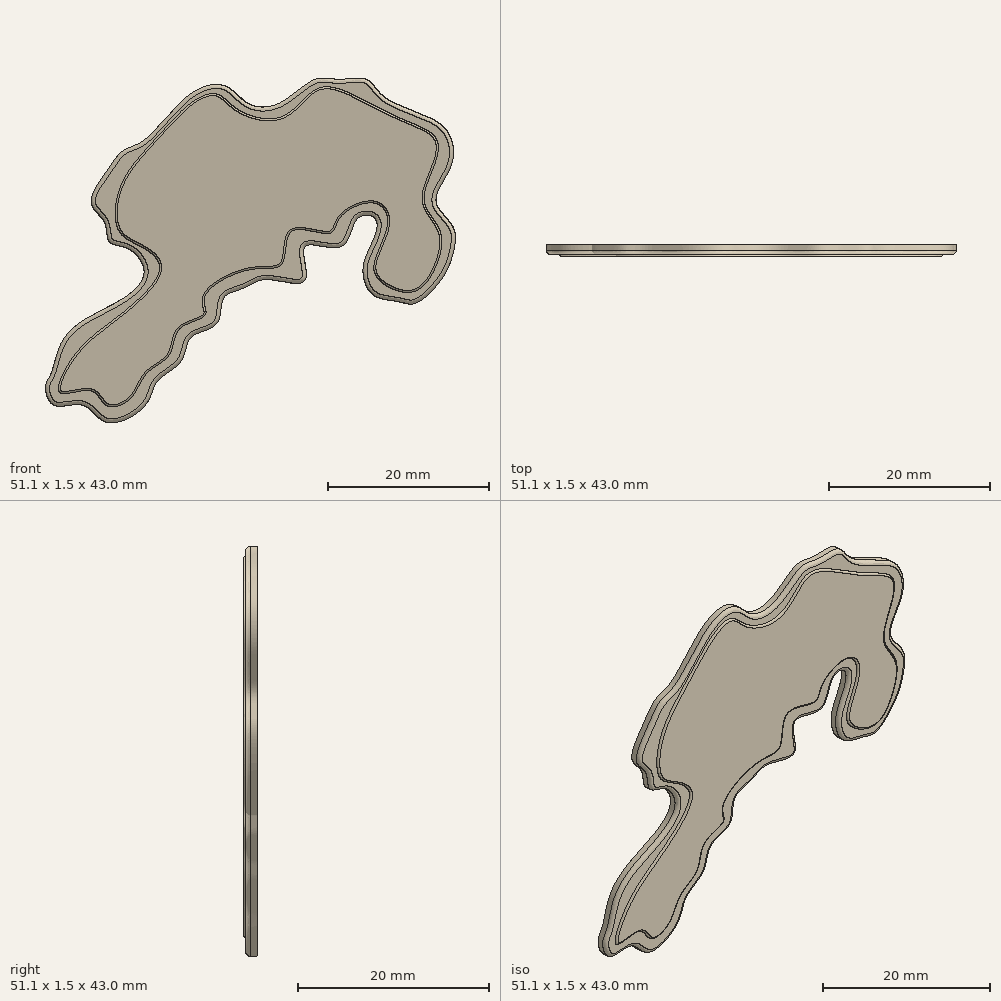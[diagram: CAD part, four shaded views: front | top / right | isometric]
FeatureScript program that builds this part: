
annotation { "Feature Type Name" : "Feature", "Feature Type Description" : "" }
export const myFeature = defineFeature(function(context is Context, id is Id, definition is map)
    precondition{}
    {
        {
            var Q0;
            Q0=qCreatedBy(makeId("Front.planeOp"),FACE);
            var sketch = newSketch(context, id + "F0", { "sketchPlane" : qUnion([Q0])});
            skFitSpline(sketch, "E0", {"points": [v(-60.38, 60.95) * mm, v(-54.67, 66.66) * mm, v(-50.23, 67.72) * mm, v(-47.48, 65.6) * mm, v(-43.46, 65.6) * mm, v(-39.02, 68.57) * mm, v(-36.06, 68.57) * mm, v(-32.68, 68.57) * mm, v(-30.56, 66.45) * mm, v(-24.64, 63.7) * mm, v(-22.32, 61.59) * mm, v(-22.1, 57.78) * mm, v(-24, 53.34) * mm, v(-21.9, 50.17) * mm, v(-21.9, 46.78) * mm, v(-23.16, 43.82) * mm, v(-26.55, 40.65) * mm, v(-28.66, 40.86) * mm, v(-31.83, 41.7) * mm, v(-33.1, 45.1) * mm, v(-31.83, 48.48) * mm, v(-31.62, 51.23) * mm, v(-33.74, 51.23) * mm, v(-35.8, 47.7) * mm, v(-40.3, 47.7) * mm, v(-40.3, 43.52) * mm, v(-45.02, 43.63) * mm, v(-47.84, 42.58) * mm, v(-50.44, 41.29) * mm, v(-51.29, 38.11) * mm, v(-54.46, 36.42) * mm, v(-55.73, 33.46) * mm, v(-58.69, 30.92) * mm, v(-60.17, 27.96) * mm, v(-65.03, 25.85) * mm, v(-68, 27.96) * mm, v(-71.59, 27.96) * mm, v(-72.64, 30.3) * mm, v(-72.01, 31.77) * mm, v(-70.74, 35.58) * mm, v(-67.57, 38.75) * mm, v(-62.92, 41.29) * mm, v(-60.38, 44.46) * mm, v(-62.28, 47.42) * mm, v(-64.7, 48.34) * mm, v(-65.32, 50.75) * mm, v(-66.94, 53.13) * mm, v(-65, 57.13) * mm, v(-62.92, 59.68) * mm, v(-60.38, 60.95) * mm]});
            skFitSpline(sketch, "E1", {"points": [v(-58.91, 61.15) * mm, v(-54.3, 65.76) * mm, v(-51.27, 66.73) * mm, v(-48.84, 64.9) * mm, v(-43.14, 63.94) * mm, v(-38.9, 67.33) * mm, v(-35.02, 66.97) * mm, v(-28.71, 63.82) * mm, v(-23.98, 61.15) * mm, v(-24.47, 57.13) * mm, v(-25.44, 53.13) * mm, v(-23.5, 49.63) * mm, v(-24.1, 45.02) * mm, v(-26.77, 42.1) * mm, v(-30.53, 43.08) * mm, v(-31.74, 45.38) * mm, v(-30.05, 50.6) * mm, v(-31.62, 53.13) * mm, v(-35.99, 51.23) * mm, v(-37.2, 49.38) * mm, v(-41.93, 49.63) * mm, v(-43.14, 45.62) * mm, v(-46.9, 44.9) * mm, v(-52.85, 41.29) * mm, v(-52.73, 39.2) * mm, v(-55.88, 37.5) * mm, v(-57.21, 34.22) * mm, v(-60, 31.92) * mm, v(-62.06, 28.77) * mm, v(-65, 27.92) * mm, v(-66.94, 29.74) * mm, v(-70.8, 29.5) * mm, v(-70.19, 32.4) * mm, v(-66.94, 36.42) * mm, v(-62.3, 40.05) * mm, v(-58.43, 45.14) * mm, v(-60.73, 47.7) * mm, v(-63.4, 49.5) * mm, v(-63.88, 53.13) * mm, v(-62.28, 57.13) * mm, v(-58.91, 61.15) * mm]});
            skSolve(sketch);
        }
        {
            var Q0;
            Q0=makeQuery(id+"F0.imprint","IMPRINT",FACE,{"disambiguationData":[TD([[makeQuery(id+"F0.imprint","IMPRINT",EDGE,{"derivedFrom":sQuery(id+"F0.wireOp",EDGE,"E0")}),-1.0]])]});
            extrude(context, id + "F1", {"entities" : qUnion([Q0]), "depth" : 1.27 * mm, "offsetDistance" : 25.4 * mm});
        }
        {
            var Q0;
            Q0=makeQuery(id+"F1.opExtrude","CAP_EDGE",EDGE,{"disambiguationData":[OSD([sQuery(id+"F0.wireOp",EDGE,"E0")])],"isStart":false});
            fillet(context, id + "F2", {"entities" : qUnion([Q0]), "radius" : 0.5 * mm, "tangentPropagation" : true, "allowEdgeOverflow" : false});
        }
        {
            var Q0;
            Q0=makeQuery(id+"F0.imprint","IMPRINT",FACE,{"disambiguationData":[TD([[makeQuery(id+"F0.imprint","IMPRINT",EDGE,{"derivedFrom":sQuery(id+"F0.wireOp",EDGE,"E1")}),-1.0]])]});
            extrude(context, id + "F3", {"entities" : qUnion([Q0]), "operationType" : NewBodyOperationType.ADD, "depth" : 1.52 * mm, "offsetDistance" : 25.4 * mm});
        }
        {
            var Q0;
            Q0=makeQuery(id+"F3.opExtrude","CAP_EDGE",EDGE,{"disambiguationData":[OSD([sQuery(id+"F0.wireOp",EDGE,"E1")])],"isStart":false});
            fillet(context, id + "F4", {"entities" : qUnion([Q0]), "radius" : 0.25 * mm, "tangentPropagation" : true, "allowEdgeOverflow" : false});
        }
    });
